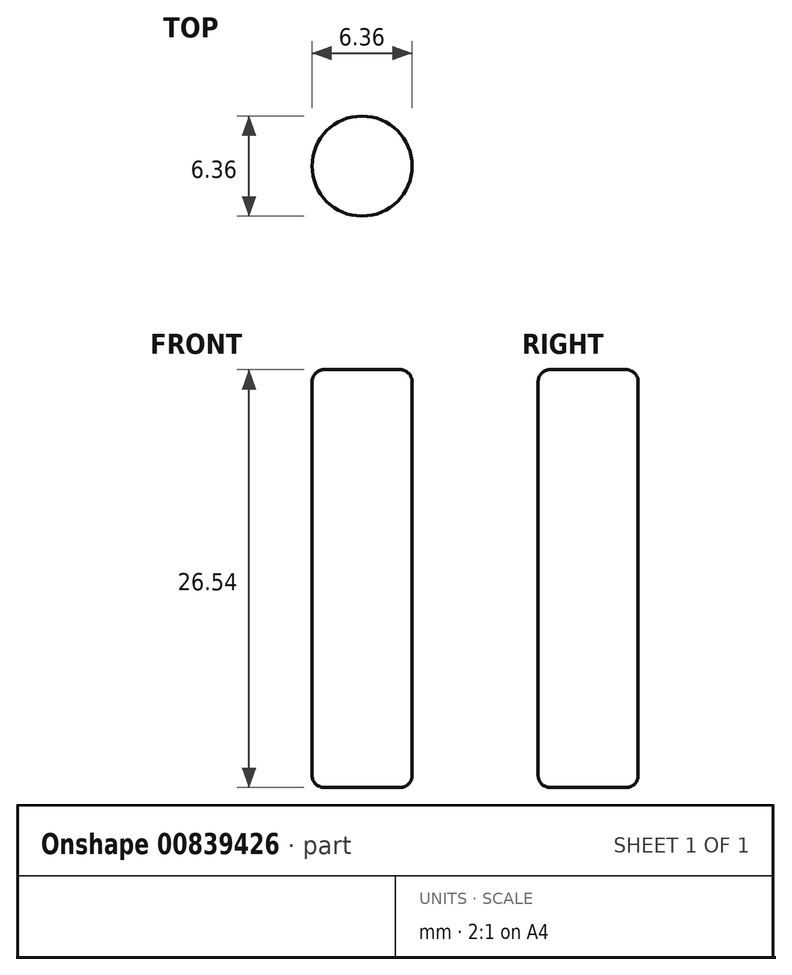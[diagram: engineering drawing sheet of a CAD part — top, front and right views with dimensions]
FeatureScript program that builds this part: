
annotation { "Feature Type Name" : "Feature", "Feature Type Description" : "" }
export const myFeature = defineFeature(function(context is Context, id is Id, definition is map)
    precondition{}
    {
        {
            var Q0;
            Q0=qCreatedBy(makeId("Top.planeOp"),FACE);
            var sketch = newSketch(context, id + "F0", { "sketchPlane" : qUnion([Q0])});
            skCircle(sketch, "E0", {"center": v(0, 0) * mm, "radius": 3.18 * mm});
            skSolve(sketch);
        }
        {
            var Q0;
            Q0 = qSketchRegion(id + "F0", true);
            extrude(context, id + "F1", {"entities" : qUnion([Q0]), "depth" : 26.54 * mm, "offsetDistance" : 25.4 * mm});
        }
        {
            var Q0;
            Q0=makeQuery(id+"F1.opExtrude","CAP_EDGE",EDGE,{"disambiguationData":[OSD([sQuery(id+"F0.wireOp",EDGE,"E0")])],"isStart":false});
            var Q1;
            Q1=makeQuery(id+"F1.opExtrude","CAP_EDGE",EDGE,{"disambiguationData":[OSD([sQuery(id+"F0.wireOp",EDGE,"E0")])],"isStart":true});
            fillet(context, id + "F2", {"entities" : qUnion([Q0, Q1]), "tangentPropagation" : true, "radius" : 0.76 * mm, "defaultsChanged" : true, "vertexSettings" : [], "allowEdgeOverflow" : false});
        }
    });
